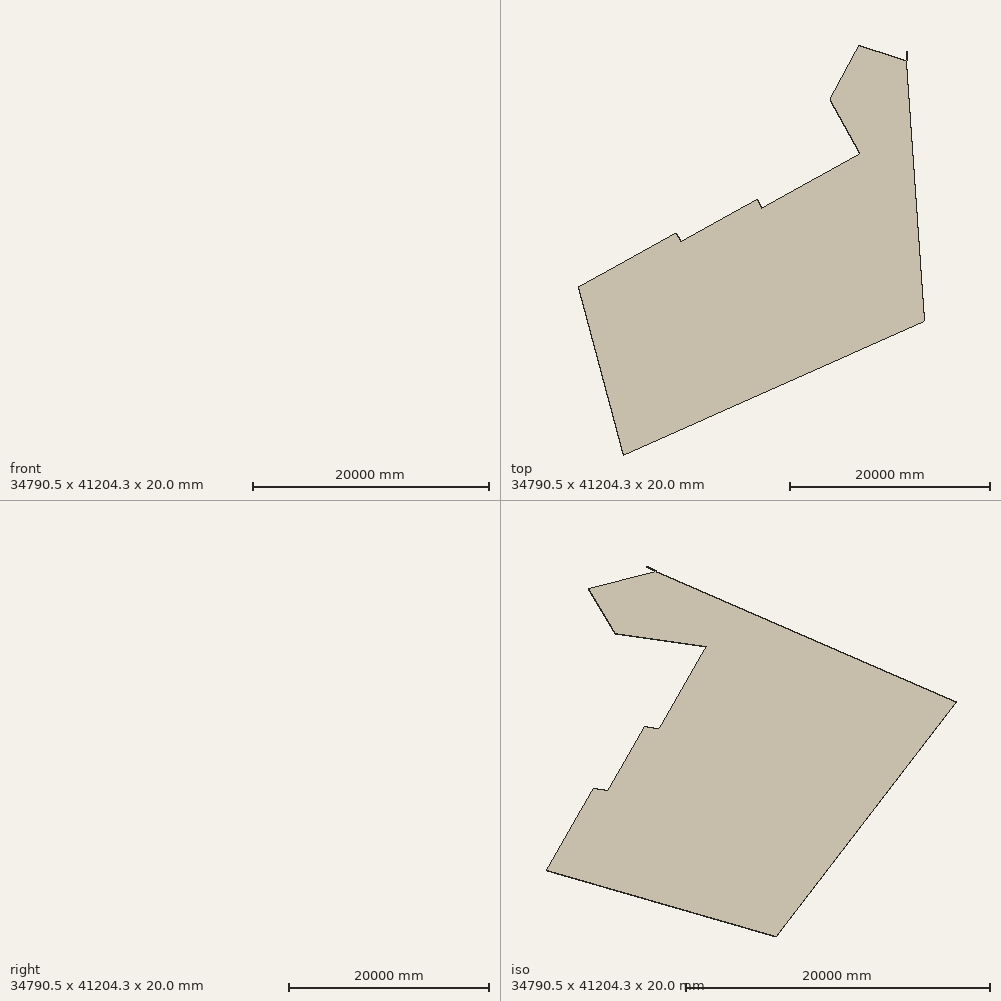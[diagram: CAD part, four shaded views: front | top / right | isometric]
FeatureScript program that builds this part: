
annotation { "Feature Type Name" : "Feature", "Feature Type Description" : "" }
export const myFeature = defineFeature(function(context is Context, id is Id, definition is map)
    precondition{}
    {
        {
            var Q0;
            Q0=qCreatedBy(makeId("Top.planeOp"),FACE);
            var sketch = newSketch(context, id + "F0", { "sketchPlane" : qUnion([Q0])});
            skLineSegment(sketch, "E0", {"start": v(1831.1, -26186.06) * mm, "end": v(-28430.09, -39659.2) * mm});
            skLineSegment(sketch, "E1", {"start": v(-28430.09, -39659.2) * mm, "end": v(-32959.42, -22755.5) * mm});
            skLineSegment(sketch, "E2", {"start": v(-32959.42, -22755.5) * mm, "end": v(-23119.95, -17301.4) * mm});
            skLineSegment(sketch, "E3", {"start": v(-23119.95, -17301.4) * mm, "end": v(-22635.14, -18176.02) * mm});
            skLineSegment(sketch, "E4", {"start": v(-22635.14, -18176.02) * mm, "end": v(-14982.22, -13933.93) * mm});
            skLineSegment(sketch, "E5", {"start": v(0, 0) * mm, "end": v(0, -10000) * mm, "construction": true});
            skLineSegment(sketch, "E6", {"start": v(3.5, -50) * mm, "end": v(1831.1, -26186.06) * mm});
            skLineSegment(sketch, "E7", {"start": v(-14982.22, -13933.93) * mm, "end": v(-14497.4, -14808.55) * mm});
            skLineSegment(sketch, "E8", {"start": v(-14497.4, -14808.55) * mm, "end": v(-4657.93, -9354.44) * mm});
            skLineSegment(sketch, "E9", {"start": v(-4657.93, -9354.44) * mm, "end": v(-7688, -3888.07) * mm});
            skLineSegment(sketch, "E10", {"start": v(0, 0) * mm, "end": v(-4755.28, 1545.08) * mm});
            skLineSegment(sketch, "E11", {"start": v(-4755.28, 1545.08) * mm, "end": v(-7688, -3888.07) * mm});
            skLineSegment(sketch, "E12.top", {"start": v(0, 950) * mm, "end": v(100, 950) * mm});
            skLineSegment(sketch, "E12.left", {"start": v(0, 0) * mm, "end": v(0, 950) * mm});
            skLineSegment(sketch, "E12.right", {"start": v(100, -50) * mm, "end": v(100, 950) * mm});
            skLineSegment(sketch, "E13", {"start": v(100, -50) * mm, "end": v(3.5, -50) * mm});
            skSolve(sketch);
        }
        {
            var Q0;
            Q0=makeQuery(id+"F0.imprint","IMPRINT",FACE,{"disambiguationData":[TD([[makeQuery(id+"F0.imprint","IMPRINT",EDGE,{"derivedFrom":sQuery(id+"F0.wireOp",EDGE,"E0")}),-1.0]])]});
            extrude(context, id + "F1", {"entities" : qUnion([Q0]), "depth" : 20 * mm, "offsetDistance" : 25 * mm});
        }
    });
